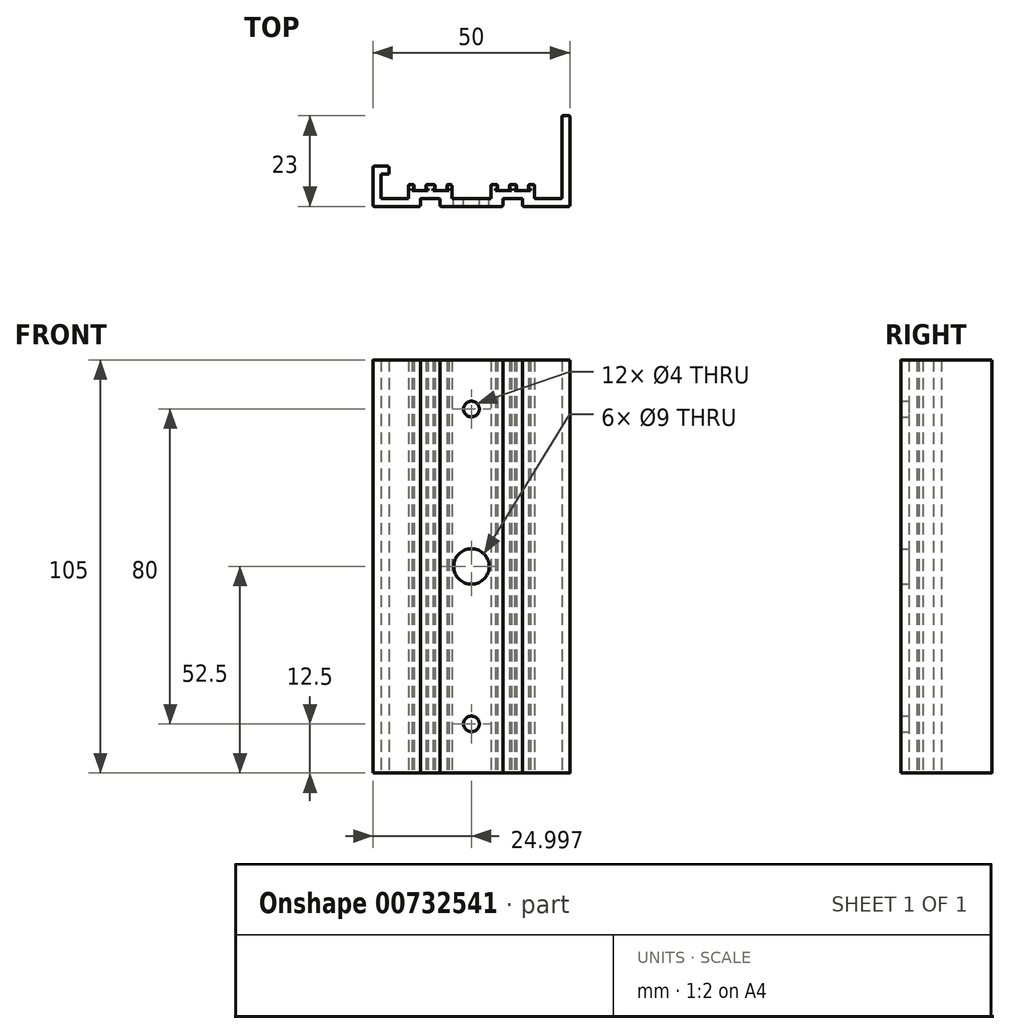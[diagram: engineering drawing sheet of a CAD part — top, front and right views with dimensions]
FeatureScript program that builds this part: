
annotation { "Feature Type Name" : "Feature", "Feature Type Description" : "" }
export const myFeature = defineFeature(function(context is Context, id is Id, definition is map)
    precondition{}
    {
        {
            var Q0;
            Q0=qCreatedBy(makeId("Top.planeOp"),FACE);
            var sketch = newSketch(context, id + "F0", { "sketchPlane" : qUnion([Q0])});
            skLineSegment(sketch, "E0", {"start": v(-30.08, -5.5) * mm, "end": v(-18.08, -5.5) * mm});
            skLineSegment(sketch, "E1", {"start": v(19.92, -5.5) * mm, "end": v(19.92, 17.5) * mm});
            skLineSegment(sketch, "E2", {"start": v(19.92, 17.5) * mm, "end": v(17.92, 17.5) * mm});
            skLineSegment(sketch, "E3", {"start": v(17.92, 17.5) * mm, "end": v(17.92, -3.5) * mm});
            skLineSegment(sketch, "E4", {"start": v(17.92, -3.5) * mm, "end": v(10.92, -3.5) * mm});
            skLineSegment(sketch, "E5", {"start": v(10.92, -3.5) * mm, "end": v(10.92, 0) * mm});
            skLineSegment(sketch, "E6", {"start": v(10.92, 0) * mm, "end": v(9.4, 0) * mm});
            skLineSegment(sketch, "E7", {"start": v(-0.08, 0) * mm, "end": v(-0.08, -3.5) * mm});
            skLineSegment(sketch, "E8", {"start": v(-0.08, -3.5) * mm, "end": v(-10.08, -3.5) * mm});
            skLineSegment(sketch, "E9", {"start": v(-10.08, -3.5) * mm, "end": v(-10.08, 0) * mm});
            skLineSegment(sketch, "E10", {"start": v(-10.08, 0) * mm, "end": v(-11.34, 0) * mm});
            skLineSegment(sketch, "E11", {"start": v(-21.08, 0) * mm, "end": v(-21.08, -3.5) * mm});
            skLineSegment(sketch, "E12", {"start": v(-21.08, -3.5) * mm, "end": v(-28.08, -3.5) * mm});
            skLineSegment(sketch, "E13", {"start": v(-28.08, -3.5) * mm, "end": v(-28.08, 2.67) * mm});
            skLineSegment(sketch, "E14", {"start": v(-28.08, 2.67) * mm, "end": v(-26.08, 2.67) * mm});
            skLineSegment(sketch, "E15", {"start": v(-26.08, 2.67) * mm, "end": v(-26.08, 4.67) * mm});
            skLineSegment(sketch, "E16", {"start": v(-26.08, 4.67) * mm, "end": v(-30.08, 4.67) * mm});
            skLineSegment(sketch, "E17", {"start": v(-30.08, 4.67) * mm, "end": v(-30.08, -5.5) * mm});
            skLineSegment(sketch, "E18", {"start": v(7.92, -5.5) * mm, "end": v(7.92, -3.5) * mm});
            skLineSegment(sketch, "E19", {"start": v(7.92, -3.5) * mm, "end": v(2.92, -3.5) * mm});
            skLineSegment(sketch, "E20", {"start": v(2.92, -3.5) * mm, "end": v(2.92, -5.5) * mm});
            skLineSegment(sketch, "E21.trimOffspring", {"start": v(7.92, -5.5) * mm, "end": v(19.92, -5.5) * mm});
            skLineSegment(sketch, "E22", {"start": v(-13.08, -5.5) * mm, "end": v(-13.08, -3.5) * mm});
            skLineSegment(sketch, "E23", {"start": v(-13.08, -3.5) * mm, "end": v(-18.08, -3.5) * mm});
            skLineSegment(sketch, "E24", {"start": v(-18.08, -3.5) * mm, "end": v(-18.08, -5.5) * mm});
            skLineSegment(sketch, "E25.trimOffspring", {"start": v(-13.08, -5.5) * mm, "end": v(2.92, -5.5) * mm});
            skLineSegment(sketch, "E26.bottom", {"start": v(-20.17, -1) * mm, "end": v(-19.67, -1) * mm});
            skLineSegment(sketch, "E26.top", {"start": v(-20.17, -1.5) * mm, "end": v(-16.17, -1.5) * mm});
            skLineSegment(sketch, "E26.left", {"start": v(-20.17, -1) * mm, "end": v(-20.17, -1.5) * mm});
            skLineSegment(sketch, "E26.right", {"start": v(-16.17, -1) * mm, "end": v(-16.17, -1.5) * mm});
            skLineSegment(sketch, "E27.bottom", {"start": v(-14.84, -1) * mm, "end": v(-14.34, -1) * mm});
            skLineSegment(sketch, "E27.top", {"start": v(-14.84, -1.5) * mm, "end": v(-10.84, -1.5) * mm});
            skLineSegment(sketch, "E27.left", {"start": v(-14.84, -1) * mm, "end": v(-14.84, -1.5) * mm});
            skLineSegment(sketch, "E27.right", {"start": v(-10.84, -1) * mm, "end": v(-10.84, -1.5) * mm});
            skLineSegment(sketch, "E28", {"start": v(-11.34, 0) * mm, "end": v(-11.34, -1) * mm});
            skLineSegment(sketch, "E29", {"start": v(-14.34, -1) * mm, "end": v(-14.34, 0) * mm});
            skLineSegment(sketch, "E30", {"start": v(-16.67, -1) * mm, "end": v(-16.67, 0) * mm});
            skLineSegment(sketch, "E31", {"start": v(-19.67, -1) * mm, "end": v(-19.67, 0) * mm});
            skLineSegment(sketch, "E32.trimOffspring", {"start": v(-19.67, 0) * mm, "end": v(-21.08, 0) * mm});
            skLineSegment(sketch, "E33.trimOffspring", {"start": v(-16.67, -1) * mm, "end": v(-16.17, -1) * mm});
            skLineSegment(sketch, "E34.trimOffspring", {"start": v(-14.34, 0) * mm, "end": v(-16.67, 0) * mm});
            skLineSegment(sketch, "E35.trimOffspring", {"start": v(-11.34, -1) * mm, "end": v(-10.84, -1) * mm});
            skLineSegment(sketch, "E36.bottom", {"start": v(1.06, -1) * mm, "end": v(1.56, -1) * mm});
            skLineSegment(sketch, "E36.top", {"start": v(1.06, -1.5) * mm, "end": v(5.06, -1.5) * mm});
            skLineSegment(sketch, "E36.left", {"start": v(1.06, -1) * mm, "end": v(1.06, -1.5) * mm});
            skLineSegment(sketch, "E36.right", {"start": v(5.06, -1) * mm, "end": v(5.06, -1.5) * mm});
            skLineSegment(sketch, "E37.bottom", {"start": v(5.9, -1) * mm, "end": v(6.4, -1) * mm});
            skLineSegment(sketch, "E37.top", {"start": v(5.9, -1.5) * mm, "end": v(9.9, -1.5) * mm});
            skLineSegment(sketch, "E37.left", {"start": v(5.9, -1) * mm, "end": v(5.9, -1.5) * mm});
            skLineSegment(sketch, "E37.right", {"start": v(9.9, -1) * mm, "end": v(9.9, -1.5) * mm});
            skLineSegment(sketch, "E38", {"start": v(1.56, 0) * mm, "end": v(1.56, -1) * mm});
            skLineSegment(sketch, "E39", {"start": v(4.56, -1) * mm, "end": v(4.56, 0) * mm});
            skLineSegment(sketch, "E40", {"start": v(6.4, -1) * mm, "end": v(6.4, 0) * mm});
            skLineSegment(sketch, "E41", {"start": v(9.4, -1) * mm, "end": v(9.4, 0) * mm});
            skLineSegment(sketch, "E42.trimOffspring", {"start": v(4.56, -1) * mm, "end": v(5.06, -1) * mm});
            skLineSegment(sketch, "E43.trimOffspring", {"start": v(9.4, -1) * mm, "end": v(9.9, -1) * mm});
            skLineSegment(sketch, "E44.trimOffspring", {"start": v(6.4, 0) * mm, "end": v(4.56, 0) * mm});
            skLineSegment(sketch, "E45.trimOffspring", {"start": v(1.56, 0) * mm, "end": v(-0.08, 0) * mm});
            skSolve(sketch);
        }
        {
            var Q0;
            Q0 = qSketchRegion(id + "F0", true);
            extrude(context, id + "F1", {"entities" : qUnion([Q0]), "depth" : 105 * mm, "offsetDistance" : 25 * mm});
        }
        {
            var Q0;
            Q0=makeQuery(id+"F1.opExtrude","SWEPT_EDGE",EDGE,{"disambiguationData":[OSD([sQuery(id+"F0.wireOp",EDGE,"E11"),sQuery(id+"F0.wireOp",EDGE,"E32.trimOffspring")])]});
            var Q1;
            Q1=makeQuery(id+"F1.opExtrude","SWEPT_EDGE",EDGE,{"disambiguationData":[OSD([sQuery(id+"F0.wireOp",EDGE,"E16"),sQuery(id+"F0.wireOp",EDGE,"E17")])]});
            var Q2;
            Q2=makeQuery(id+"F1.opExtrude","SWEPT_EDGE",EDGE,{"disambiguationData":[OSD([sQuery(id+"F0.wireOp",EDGE,"E15"),sQuery(id+"F0.wireOp",EDGE,"E16")])]});
            var Q3;
            Q3=makeQuery(id+"F1.opExtrude","SWEPT_EDGE",EDGE,{"disambiguationData":[OSD([sQuery(id+"F0.wireOp",EDGE,"E31"),sQuery(id+"F0.wireOp",EDGE,"E32.trimOffspring")])]});
            var Q4;
            Q4=makeQuery(id+"F1.opExtrude","SWEPT_EDGE",EDGE,{"disambiguationData":[OSD([sQuery(id+"F0.wireOp",EDGE,"E30"),sQuery(id+"F0.wireOp",EDGE,"E34.trimOffspring")])]});
            var Q5;
            Q5=makeQuery(id+"F1.opExtrude","SWEPT_EDGE",EDGE,{"disambiguationData":[OSD([sQuery(id+"F0.wireOp",EDGE,"E29"),sQuery(id+"F0.wireOp",EDGE,"E34.trimOffspring")])]});
            var Q6;
            Q6=makeQuery(id+"F1.opExtrude","SWEPT_EDGE",EDGE,{"disambiguationData":[OSD([sQuery(id+"F0.wireOp",EDGE,"E10"),sQuery(id+"F0.wireOp",EDGE,"E28")])]});
            var Q7;
            Q7=makeQuery(id+"F1.opExtrude","SWEPT_EDGE",EDGE,{"disambiguationData":[OSD([sQuery(id+"F0.wireOp",EDGE,"E9"),sQuery(id+"F0.wireOp",EDGE,"E10")])]});
            var Q8;
            Q8=makeQuery(id+"F1.opExtrude","SWEPT_EDGE",EDGE,{"disambiguationData":[OSD([sQuery(id+"F0.wireOp",EDGE,"E7"),sQuery(id+"F0.wireOp",EDGE,"E45.trimOffspring")])]});
            var Q9;
            Q9=makeQuery(id+"F1.opExtrude","SWEPT_EDGE",EDGE,{"disambiguationData":[OSD([sQuery(id+"F0.wireOp",EDGE,"E38"),sQuery(id+"F0.wireOp",EDGE,"E45.trimOffspring")])]});
            var Q10;
            Q10=makeQuery(id+"F1.opExtrude","SWEPT_EDGE",EDGE,{"disambiguationData":[OSD([sQuery(id+"F0.wireOp",EDGE,"E39"),sQuery(id+"F0.wireOp",EDGE,"E44.trimOffspring")])]});
            var Q11;
            Q11=makeQuery(id+"F1.opExtrude","SWEPT_EDGE",EDGE,{"disambiguationData":[OSD([sQuery(id+"F0.wireOp",EDGE,"E40"),sQuery(id+"F0.wireOp",EDGE,"E44.trimOffspring")])]});
            var Q12;
            Q12=makeQuery(id+"F1.opExtrude","SWEPT_EDGE",EDGE,{"disambiguationData":[OSD([sQuery(id+"F0.wireOp",EDGE,"E6"),sQuery(id+"F0.wireOp",EDGE,"E41")])]});
            var Q13;
            Q13=makeQuery(id+"F1.opExtrude","SWEPT_EDGE",EDGE,{"disambiguationData":[OSD([sQuery(id+"F0.wireOp",EDGE,"E5"),sQuery(id+"F0.wireOp",EDGE,"E6")])]});
            var Q14;
            Q14=makeQuery(id+"F1.opExtrude","SWEPT_EDGE",EDGE,{"disambiguationData":[OSD([sQuery(id+"F0.wireOp",EDGE,"E2"),sQuery(id+"F0.wireOp",EDGE,"E3")])]});
            var Q15;
            Q15=makeQuery(id+"F1.opExtrude","SWEPT_EDGE",EDGE,{"disambiguationData":[OSD([sQuery(id+"F0.wireOp",EDGE,"E0"),sQuery(id+"F0.wireOp",EDGE,"E17")])]});
            var Q16;
            Q16=makeQuery(id+"F1.opExtrude","SWEPT_EDGE",EDGE,{"disambiguationData":[OSD([sQuery(id+"F0.wireOp",EDGE,"E1"),sQuery(id+"F0.wireOp",EDGE,"E2")])]});
            var Q17;
            Q17=makeQuery(id+"F1.opExtrude","SWEPT_EDGE",EDGE,{"disambiguationData":[OSD([sQuery(id+"F0.wireOp",EDGE,"E4"),sQuery(id+"F0.wireOp",EDGE,"E5")])]});
            var Q18;
            Q18=makeQuery(id+"F1.opExtrude","SWEPT_EDGE",EDGE,{"disambiguationData":[OSD([sQuery(id+"F0.wireOp",EDGE,"E3"),sQuery(id+"F0.wireOp",EDGE,"E4")])]});
            var Q19;
            Q19=makeQuery(id+"F1.opExtrude","SWEPT_EDGE",EDGE,{"disambiguationData":[OSD([sQuery(id+"F0.wireOp",EDGE,"E1"),sQuery(id+"F0.wireOp",EDGE,"E21.trimOffspring")])]});
            var Q20;
            Q20=makeQuery(id+"F1.opExtrude","SWEPT_EDGE",EDGE,{"disambiguationData":[OSD([sQuery(id+"F0.wireOp",EDGE,"E20"),sQuery(id+"F0.wireOp",EDGE,"E25.trimOffspring")])]});
            var Q21;
            Q21=makeQuery(id+"F1.opExtrude","SWEPT_EDGE",EDGE,{"disambiguationData":[OSD([sQuery(id+"F0.wireOp",EDGE,"E18"),sQuery(id+"F0.wireOp",EDGE,"E21.trimOffspring")])]});
            var Q22;
            Q22=makeQuery(id+"F1.opExtrude","SWEPT_EDGE",EDGE,{"disambiguationData":[OSD([sQuery(id+"F0.wireOp",EDGE,"E22"),sQuery(id+"F0.wireOp",EDGE,"E25.trimOffspring")])]});
            var Q23;
            Q23=makeQuery(id+"F1.opExtrude","SWEPT_EDGE",EDGE,{"disambiguationData":[OSD([sQuery(id+"F0.wireOp",EDGE,"E0"),sQuery(id+"F0.wireOp",EDGE,"E24")])]});
            var Q24;
            Q24=makeQuery(id+"F1.opExtrude","SWEPT_EDGE",EDGE,{"disambiguationData":[OSD([sQuery(id+"F0.wireOp",EDGE,"E23"),sQuery(id+"F0.wireOp",EDGE,"E24")])]});
            var Q25;
            Q25=makeQuery(id+"F1.opExtrude","SWEPT_EDGE",EDGE,{"disambiguationData":[OSD([sQuery(id+"F0.wireOp",EDGE,"E22"),sQuery(id+"F0.wireOp",EDGE,"E23")])]});
            var Q26;
            Q26=makeQuery(id+"F1.opExtrude","SWEPT_EDGE",EDGE,{"disambiguationData":[OSD([sQuery(id+"F0.wireOp",EDGE,"E19"),sQuery(id+"F0.wireOp",EDGE,"E20")])]});
            var Q27;
            Q27=makeQuery(id+"F1.opExtrude","SWEPT_EDGE",EDGE,{"disambiguationData":[OSD([sQuery(id+"F0.wireOp",EDGE,"E18"),sQuery(id+"F0.wireOp",EDGE,"E19")])]});
            fillet(context, id + "F2", {"entities" : qUnion([Q0, Q1, Q2, Q3, Q4, Q5, Q6, Q7, Q8, Q9, Q10, Q11, Q12, Q13, Q14, Q15, Q16, Q17, Q18, Q19, Q20, Q21, Q22, Q23, Q24, Q25, Q26, Q27]), "radius" : 0.25 * mm, "tangentPropagation" : true, "allowEdgeOverflow" : false});
        }
        {
            var Q0;
            Q0=makeQuery(id+"F1.opExtrude","SWEPT_FACE",FACE,{"disambiguationData":[OSD([sQuery(id+"F0.wireOp",EDGE,"E8")])]});
            var sketch = newSketch(context, id + "F3", { "sketchPlane" : qUnion([Q0])});
            skLineSegment(sketch, "E46", {"start": v(5.08, 105) * mm, "end": v(5.08, 0) * mm, "construction": true});
            skCircle(sketch, "E47", {"center": v(5.08, 92.5) * mm, "radius": 2 * mm});
            skCircle(sketch, "E48", {"center": v(5.08, 12.5) * mm, "radius": 2 * mm});
            skCircle(sketch, "E49", {"center": v(5.08, 52.5) * mm, "radius": 4.5 * mm});
            skSolve(sketch);
        }
        {
            var Q0;
            Q0 = qSketchRegion(id + "F3", true);
            extrude(context, id + "F4", {"entities" : qUnion([Q0]), "operationType" : NewBodyOperationType.REMOVE, "oppositeDirection" : true, "depth" : 25 * mm, "offsetDistance" : 25 * mm});
        }
    });
